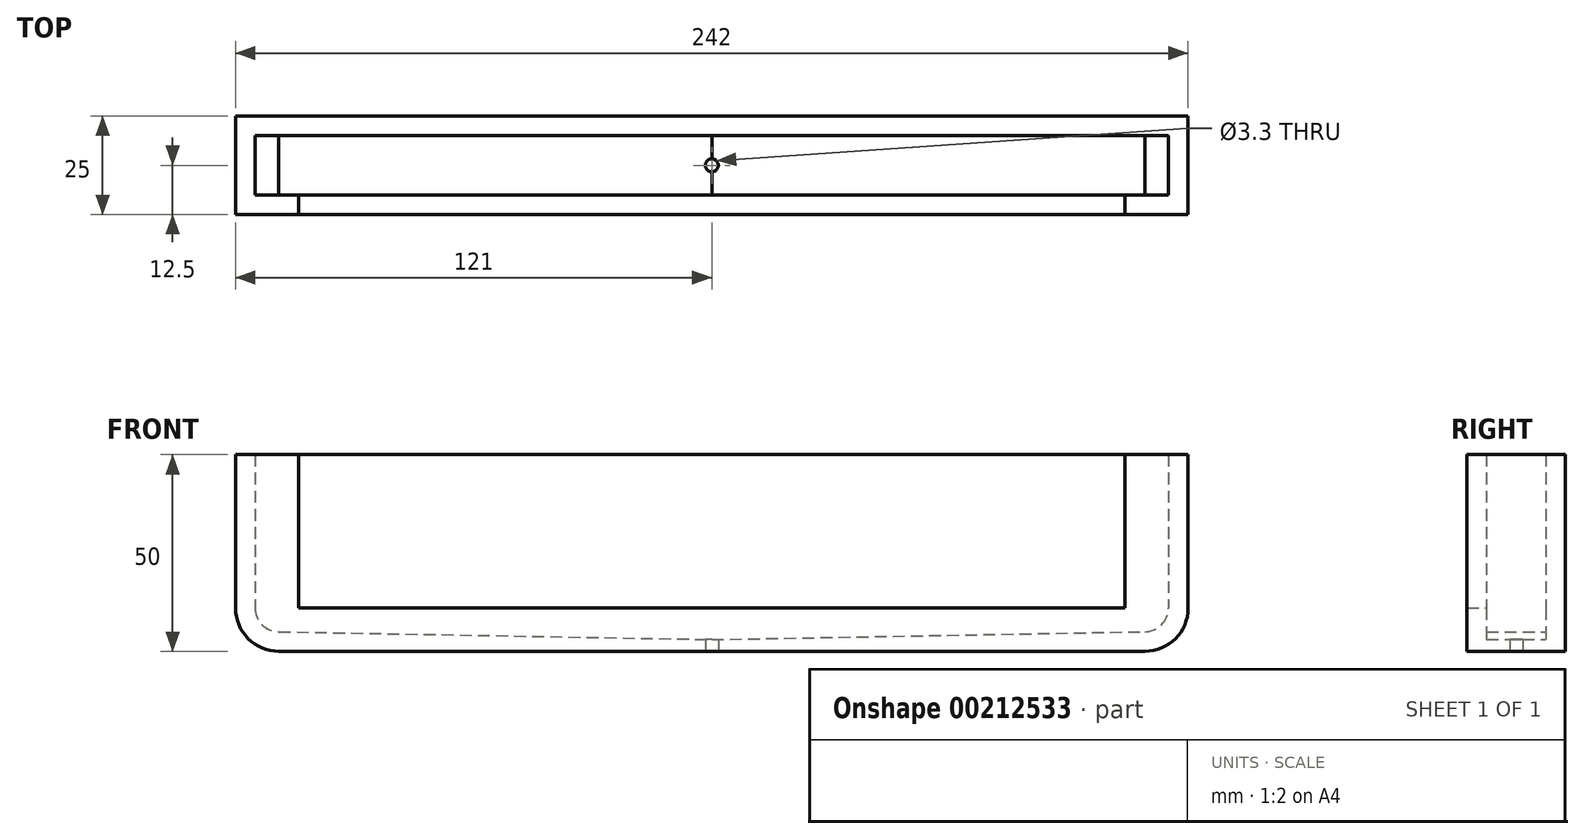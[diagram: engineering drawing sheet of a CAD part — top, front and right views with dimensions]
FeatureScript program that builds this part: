
annotation { "Feature Type Name" : "Feature", "Feature Type Description" : "" }
export const myFeature = defineFeature(function(context is Context, id is Id, definition is map)
    precondition{}
    {
        {
            var Q0;
            Q0=qCreatedBy(makeId("Front.planeOp"),FACE);
            var sketch = newSketch(context, id + "F0", { "sketchPlane" : qUnion([Q0])});
            skLineSegment(sketch, "E0.bottom", {"start": v(110, 77.5) * mm, "end": v(-110, 77.5) * mm});
            skLineSegment(sketch, "E0.top", {"start": v(110, -77.5) * mm, "end": v(-110, -77.5) * mm});
            skLineSegment(sketch, "E0.left", {"start": v(115, 72.5) * mm, "end": v(115, -72.5) * mm});
            skLineSegment(sketch, "E0.right", {"start": v(-115, 72.5) * mm, "end": v(-115, -72.5) * mm});
            skPoint(sketch, "E0.middle", {"position": v(0, 0) * mm});
            skPoint(sketch, "E1.visualSharp", {"position": v(-115, 77.5) * mm});
            skArc(sketch, "E1.filletArc", {"start": v(-110, 77.5) * mm, "mid": v(-113.54, 76.04) * mm, "end": v(-115, 72.5) * mm});
            skPoint(sketch, "E2.visualSharp", {"position": v(115, 77.5) * mm});
            skArc(sketch, "E2.filletArc", {"start": v(115, 72.5) * mm, "mid": v(113.54, 76.04) * mm, "end": v(110, 77.5) * mm});
            skPoint(sketch, "E3.visualSharp", {"position": v(115, -77.5) * mm});
            skArc(sketch, "E3.filletArc", {"start": v(110, -77.5) * mm, "mid": v(113.54, -76.04) * mm, "end": v(115, -72.5) * mm});
            skPoint(sketch, "E4.visualSharp", {"position": v(-115, -77.5) * mm});
            skArc(sketch, "E4.filletArc", {"start": v(-115, -72.5) * mm, "mid": v(-113.54, -76.04) * mm, "end": v(-110, -77.5) * mm});
            skLineSegment(sketch, "E5.0", {"start": v(116, 72.5) * mm, "end": v(116, -72.5) * mm});
            skLineSegment(sketch, "E5.1", {"start": v(-116, 72.5) * mm, "end": v(-116, -72.5) * mm});
            skArc(sketch, "E5.2", {"start": v(-116, -72.5) * mm, "mid": v(-114.24, -76.74) * mm, "end": v(-110, -78.5) * mm});
            skLineSegment(sketch, "E5.3", {"start": v(110, -78.5) * mm, "end": v(-110, -78.5) * mm});
            skArc(sketch, "E5.4", {"start": v(110, -78.5) * mm, "mid": v(114.24, -76.74) * mm, "end": v(116, -72.5) * mm});
            skLineSegment(sketch, "E6.0", {"start": v(121, 72.5) * mm, "end": v(121, -72.5) * mm});
            skLineSegment(sketch, "E6.1", {"start": v(-121, 72.5) * mm, "end": v(-121, -72.5) * mm});
            skArc(sketch, "E6.2", {"start": v(-121, -72.5) * mm, "mid": v(-117.78, -80.28) * mm, "end": v(-110, -83.5) * mm});
            skLineSegment(sketch, "E6.3", {"start": v(110, -83.5) * mm, "end": v(-110, -83.5) * mm});
            skArc(sketch, "E6.4", {"start": v(110, -83.5) * mm, "mid": v(117.78, -80.28) * mm, "end": v(121, -72.5) * mm});
            skLineSegment(sketch, "E7", {"start": v(-121, 72.5) * mm, "end": v(-116, 72.5) * mm});
            skLineSegment(sketch, "E8", {"start": v(-115, 72.5) * mm, "end": v(-116, 72.5) * mm});
            skLineSegment(sketch, "E9", {"start": v(115, 72.5) * mm, "end": v(116, 72.5) * mm});
            skLineSegment(sketch, "E10", {"start": v(121, 72.5) * mm, "end": v(116, 72.5) * mm});
            skLineSegment(sketch, "E11", {"start": v(-121, -33.5) * mm, "end": v(-116, -33.5) * mm});
            skLineSegment(sketch, "E12", {"start": v(-116, -33.5) * mm, "end": v(-115, -33.5) * mm});
            skLineSegment(sketch, "E13", {"start": v(-115, -33.5) * mm, "end": v(-105, -33.5) * mm});
            skLineSegment(sketch, "E14", {"start": v(-105, -33.5) * mm, "end": v(-105, -77.5) * mm});
            skLineSegment(sketch, "E15", {"start": v(121, -33.5) * mm, "end": v(116, -33.5) * mm});
            skLineSegment(sketch, "E16", {"start": v(116, -33.5) * mm, "end": v(115, -33.5) * mm});
            skLineSegment(sketch, "E17", {"start": v(115, -33.5) * mm, "end": v(105, -33.5) * mm});
            skPoint(sketch, "E17.endSnap0", {"position": v(118.5, -33.5) * mm});
            skLineSegment(sketch, "E18", {"start": v(105, -33.5) * mm, "end": v(105, -77.5) * mm});
            skLineSegment(sketch, "E19", {"start": v(-105, -33.5) * mm, "end": v(105, -33.5) * mm});
            skLineSegment(sketch, "E20", {"start": v(-110, -78.5) * mm, "end": v(0, -80.5) * mm});
            skPoint(sketch, "E20.endSnap0", {"position": v(0, -78.5) * mm});
            skLineSegment(sketch, "E21", {"start": v(0, -80.5) * mm, "end": v(110, -78.5) * mm});
            skLineSegment(sketch, "E22", {"start": v(-105, -72.5) * mm, "end": v(105, -72.5) * mm});
            skSolve(sketch);
        }
        {
            var Q0;
            {var subQ4=sQuery(id+"F0.wireOp",EDGE,"E5.2");Q0=makeQuery(id+"F0.imprint","IMPRINT",FACE,{"disambiguationData":[TD([[makeQuery(id+"F0.imprint","IMPRINT",EDGE,{"derivedFrom":subQ4}),-1.0]])]});}
            var Q1;
            {var subQ8=sQuery(id+"F0.wireOp",EDGE,"E3.filletArc");Q1=makeQuery(id+"F0.imprint","IMPRINT",FACE,{"disambiguationData":[TD([[makeQuery(id+"F0.imprint","IMPRINT",EDGE,{"derivedFrom":subQ8}),-1.0]])]});}
            var Q2;
            {var subQ0=sQuery(id+"F0.wireOp",EDGE,"E4.filletArc");Q2=makeQuery(id+"F0.imprint","IMPRINT",FACE,{"disambiguationData":[TD([[makeQuery(id+"F0.imprint","IMPRINT",EDGE,{"derivedFrom":subQ0}),1.0]])]});}
            var Q3;
            {var subQ0=sQuery(id+"F0.wireOp",EDGE,"E3.filletArc");Q3=makeQuery(id+"F0.imprint","IMPRINT",FACE,{"disambiguationData":[TD([[makeQuery(id+"F0.imprint","IMPRINT",EDGE,{"derivedFrom":subQ0}),1.0]])]});}
            var Q4;
            {var subQ0=sQuery(id+"F0.wireOp",EDGE,"E14");Q4=makeQuery(id+"F0.imprint","IMPRINT",FACE,{"disambiguationData":[TD([[makeQuery(id+"F0.imprint","IMPRINT",EDGE,{"derivedFrom":subQ0}),1.0]])]});}
            var Q5;
            Q5=makeQuery(id+"F0.imprint","IMPRINT",FACE,{"disambiguationData":[TD([[makeQuery(id+"F0.imprint","IMPRINT",EDGE,{"derivedFrom":sQuery(id+"F0.wireOp",EDGE,"E5.3")}),1.0]])]});
            extrude(context, id + "F1", {"entities" : qUnion([Q0, Q1, Q2, Q3, Q4, Q5]), "oppositeDirection" : true, "depth" : 5 * mm});
        }
        {
            var Q0;
            {var subQ4=sQuery(id+"F0.wireOp",EDGE,"E5.2");Q0=makeQuery(id+"F0.imprint","IMPRINT",FACE,{"disambiguationData":[TD([[makeQuery(id+"F0.imprint","IMPRINT",EDGE,{"derivedFrom":subQ4}),-1.0]])]});}
            var Q1;
            {var subQ8=sQuery(id+"F0.wireOp",EDGE,"E3.filletArc");Q1=makeQuery(id+"F0.imprint","IMPRINT",FACE,{"disambiguationData":[TD([[makeQuery(id+"F0.imprint","IMPRINT",EDGE,{"derivedFrom":subQ8}),-1.0]])]});}
            var Q2;
            {var subQ0=sQuery(id+"F0.wireOp",EDGE,"E4.filletArc");Q2=makeQuery(id+"F0.imprint","IMPRINT",FACE,{"disambiguationData":[TD([[makeQuery(id+"F0.imprint","IMPRINT",EDGE,{"derivedFrom":subQ0}),1.0]])]});}
            var Q3;
            {var subQ0=sQuery(id+"F0.wireOp",EDGE,"E3.filletArc");Q3=makeQuery(id+"F0.imprint","IMPRINT",FACE,{"disambiguationData":[TD([[makeQuery(id+"F0.imprint","IMPRINT",EDGE,{"derivedFrom":subQ0}),1.0]])]});}
            var Q4;
            Q4=makeQuery(id+"F0.imprint","IMPRINT",FACE,{"disambiguationData":[TD([[makeQuery(id+"F0.imprint","IMPRINT",EDGE,{"derivedFrom":sQuery(id+"F0.wireOp",EDGE,"E5.3")}),1.0]])]});
            var Q5;
            {var subQ5=sQuery(id+"F0.wireOp",EDGE,"E22");Q5=makeQuery(id+"F0.imprint","IMPRINT",FACE,{"disambiguationData":[TD([[makeQuery(id+"F0.imprint","IMPRINT",EDGE,{"derivedFrom":subQ5}),-1.0]])]});}
            extrude(context, id + "F2", {"entities" : qUnion([Q0, Q1, Q2, Q3, Q4, Q5]), "operationType" : NewBodyOperationType.ADD, "depth" : 20 * mm});
        }
        {
            var Q0;
            {var subQ0=sQuery(id+"F0.wireOp",EDGE,"E4.filletArc");Q0=makeQuery(id+"F0.imprint","IMPRINT",FACE,{"disambiguationData":[TD([[makeQuery(id+"F0.imprint","IMPRINT",EDGE,{"derivedFrom":subQ0}),1.0]])]});}
            var Q1;
            {var subQ8=sQuery(id+"F0.wireOp",EDGE,"E3.filletArc");Q1=makeQuery(id+"F0.imprint","IMPRINT",FACE,{"disambiguationData":[TD([[makeQuery(id+"F0.imprint","IMPRINT",EDGE,{"derivedFrom":subQ8}),-1.0]])]});}
            var Q2;
            {var subQ0=sQuery(id+"F0.wireOp",EDGE,"E3.filletArc");Q2=makeQuery(id+"F0.imprint","IMPRINT",FACE,{"disambiguationData":[TD([[makeQuery(id+"F0.imprint","IMPRINT",EDGE,{"derivedFrom":subQ0}),1.0]])]});}
            var Q3;
            Q3=makeQuery(id+"F0.imprint","IMPRINT",FACE,{"disambiguationData":[TD([[makeQuery(id+"F0.imprint","IMPRINT",EDGE,{"derivedFrom":sQuery(id+"F0.wireOp",EDGE,"E5.3")}),1.0]])]});
            var Q4;
            {var subQ5=sQuery(id+"F0.wireOp",EDGE,"E22");Q4=makeQuery(id+"F0.imprint","IMPRINT",FACE,{"disambiguationData":[TD([[makeQuery(id+"F0.imprint","IMPRINT",EDGE,{"derivedFrom":subQ5}),-1.0]])]});}
            extrude(context, id + "F3", {"entities" : qUnion([Q0, Q1, Q2, Q3, Q4]), "operationType" : NewBodyOperationType.REMOVE, "depth" : 15 * mm});
        }
        {
            var Q0;
            {var subQ0=sQuery(id+"F0.wireOp",EDGE,"E6.3");Q0=makeQuery(id+"F2.boolean.opBoolean","MERGE",FACE,{"derivedFrom":[makeQuery(id+"F1.opExtrude","SWEPT_FACE",FACE,{"disambiguationData":[OSD([subQ0])]}),makeQuery(id+"F2.opExtrude","SWEPT_FACE",FACE,{"disambiguationData":[OSD([subQ0])]})]});}
            var sketch = newSketch(context, id + "F4", { "sketchPlane" : qUnion([Q0])});
            skPoint(sketch, "E23.0", {"position": v(0, 7.5) * mm});
            skSolve(sketch);
        }
        {
            var Q0;
            Q0=sQuery(id+"F4.wireOp",VERTEX,"E23.0");
            var Q1;
            Q1=makeQuery(id+"F1.opExtrude","SWEPT_BODY",BODY,{"disambiguationData":[OSD([sQuery(id+"F0.wireOp",EDGE,"E6.0"),sQuery(id+"F0.wireOp",EDGE,"E6.1"),sQuery(id+"F0.wireOp",EDGE,"E6.2"),sQuery(id+"F0.wireOp",EDGE,"E6.3"),sQuery(id+"F0.wireOp",EDGE,"E6.4"),sQuery(id+"F0.wireOp",EDGE,"E11"),sQuery(id+"F0.wireOp",EDGE,"E12"),sQuery(id+"F0.wireOp",EDGE,"E13"),sQuery(id+"F0.wireOp",EDGE,"E15"),sQuery(id+"F0.wireOp",EDGE,"E16"),sQuery(id+"F0.wireOp",EDGE,"E17"),sQuery(id+"F0.wireOp",EDGE,"E19")])]});
            hole(context, id + "F5", {"style" : HoleStyle.SIMPLE, "endStyle" : HoleEndStyle.BLIND, "holeDiameter" : 3.3 * mm, "holeDepth" : 5 * mm, "startFromSketch" : true, "locations" : qUnion([Q0]), "scope" : qUnion([Q1])});
        }
    });
